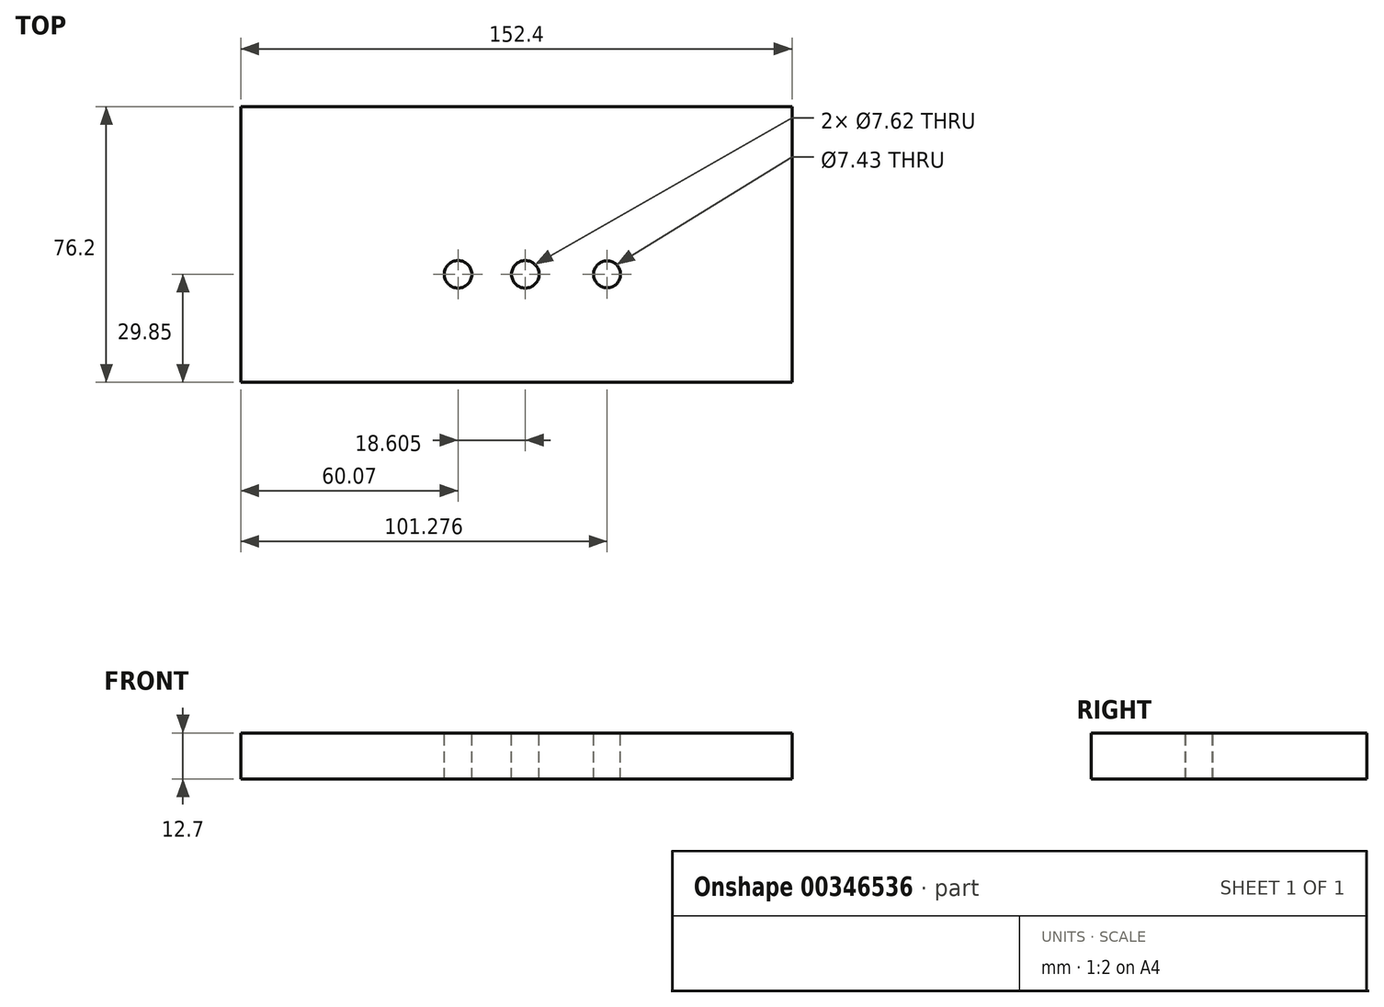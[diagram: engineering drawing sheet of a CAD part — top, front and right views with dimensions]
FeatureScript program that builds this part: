
annotation { "Feature Type Name" : "Feature", "Feature Type Description" : "" }
export const myFeature = defineFeature(function(context is Context, id is Id, definition is map)
    precondition{}
    {
        {
            var Q0;
            Q0=qCreatedBy(makeId("Top.planeOp"),FACE);
            var sketch = newSketch(context, id + "F0", { "sketchPlane" : qUnion([Q0])});
            skLineSegment(sketch, "E0.bottom", {"start": v(-60.07, 46.35) * mm, "end": v(92.33, 46.35) * mm});
            skLineSegment(sketch, "E0.top", {"start": v(-60.07, -29.85) * mm, "end": v(92.33, -29.85) * mm});
            skLineSegment(sketch, "E0.left", {"start": v(-60.07, 46.35) * mm, "end": v(-60.07, -29.85) * mm});
            skLineSegment(sketch, "E0.right", {"start": v(92.33, 46.35) * mm, "end": v(92.33, -29.85) * mm});
            skSolve(sketch);
        }
        {
            var Q0;
            Q0 = qSketchRegion(id + "F0", true);
            extrude(context, id + "F1", {"entities" : qUnion([Q0]), "depth" : 12.7 * mm});
        }
        {
            var Q0;
            Q0=makeQuery(id+"F1.opExtrude","CAP_FACE",FACE,{"disambiguationData":[OSD([sQuery(id+"F0.wireOp",EDGE,"E0.bottom"),sQuery(id+"F0.wireOp",EDGE,"E0.top"),sQuery(id+"F0.wireOp",EDGE,"E0.left"),sQuery(id+"F0.wireOp",EDGE,"E0.right")])],"isStart":false});
            var sketch = newSketch(context, id + "F2", { "sketchPlane" : qUnion([Q0])});
            skCircle(sketch, "E1", {"center": v(0, 0) * mm, "radius": 3.81 * mm});
            skSolve(sketch);
        }
        {
            var Q0;
            Q0=makeQuery(id+"F2.imprint","IMPRINT",FACE,{"disambiguationData":[TD([[makeQuery(id+"F2.imprint","IMPRINT",EDGE,{"derivedFrom":sQuery(id+"F2.wireOp",EDGE,"E1")}),1.0]])]});
            extrude(context, id + "F3", {"entities" : qUnion([Q0]), "operationType" : NewBodyOperationType.REMOVE, "oppositeDirection" : true, "depth" : 25.4 * mm});
        }
        {
            var Q0;
            Q0=makeQuery(id+"F1.opExtrude","CAP_FACE",FACE,{"disambiguationData":[OSD([sQuery(id+"F0.wireOp",EDGE,"E0.bottom"),sQuery(id+"F0.wireOp",EDGE,"E0.top"),sQuery(id+"F0.wireOp",EDGE,"E0.left"),sQuery(id+"F0.wireOp",EDGE,"E0.right")])],"isStart":false});
            var sketch = newSketch(context, id + "F4", { "sketchPlane" : qUnion([Q0])});
            skCircle(sketch, "E2", {"center": v(18.6, 0) * mm, "radius": 3.8 * mm});
            skCircle(sketch, "E3", {"center": v(41.2, 0) * mm, "radius": 3.72 * mm});
            skSolve(sketch);
        }
        {
            var Q0;
            Q0=makeQuery(id+"F4.imprint","IMPRINT",FACE,{"disambiguationData":[TD([[makeQuery(id+"F4.imprint","IMPRINT",EDGE,{"derivedFrom":sQuery(id+"F4.wireOp",EDGE,"E2")}),1.0]])]});
            var Q1;
            Q1=makeQuery(id+"F4.imprint","IMPRINT",FACE,{"disambiguationData":[TD([[makeQuery(id+"F4.imprint","IMPRINT",EDGE,{"derivedFrom":sQuery(id+"F4.wireOp",EDGE,"E3")}),1.0]])]});
            extrude(context, id + "F5", {"entities" : qUnion([Q0, Q1]), "operationType" : NewBodyOperationType.REMOVE, "endBound" : BoundingType.THROUGH_ALL, "oppositeDirection" : true, "depth" : 25.4 * mm});
        }
    });
